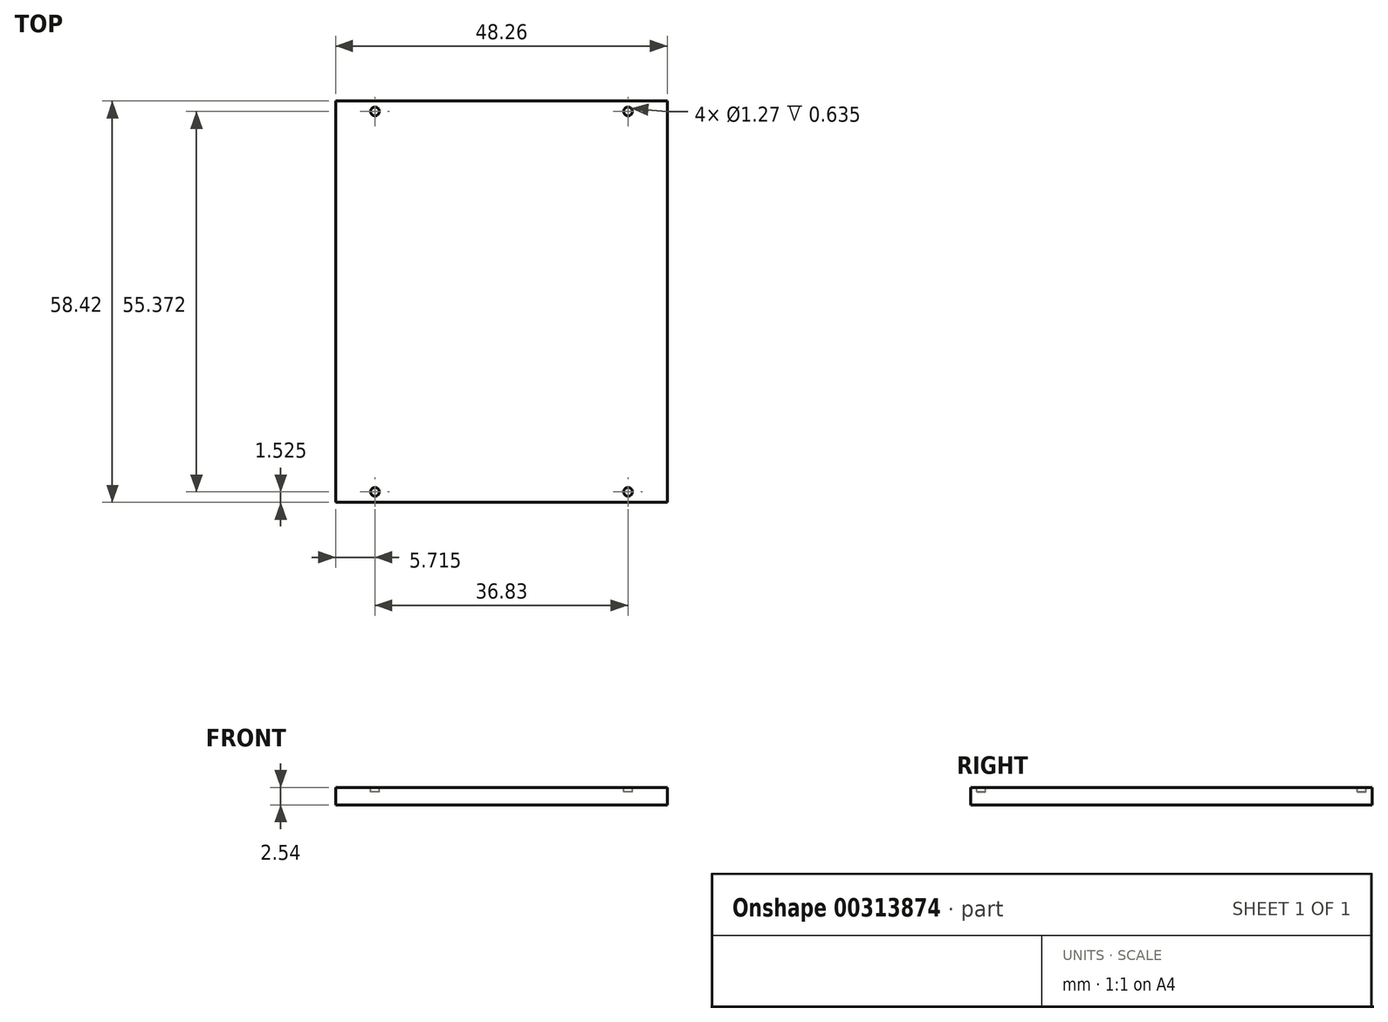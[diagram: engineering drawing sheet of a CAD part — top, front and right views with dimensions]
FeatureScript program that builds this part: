
annotation { "Feature Type Name" : "Feature", "Feature Type Description" : "" }
export const myFeature = defineFeature(function(context is Context, id is Id, definition is map)
    precondition{}
    {
        {
            var Q0;
            Q0=qCreatedBy(makeId("Top.planeOp"),FACE);
            var sketch = newSketch(context, id + "F0", { "sketchPlane" : qUnion([Q0])});
            skLineSegment(sketch, "E0.bottom", {"start": v(-22.14, 39.8) * mm, "end": v(26.12, 39.8) * mm});
            skLineSegment(sketch, "E0.top", {"start": v(-22.14, -18.62) * mm, "end": v(26.12, -18.62) * mm});
            skLineSegment(sketch, "E0.left", {"start": v(-22.14, 39.8) * mm, "end": v(-22.14, -18.62) * mm});
            skLineSegment(sketch, "E0.right", {"start": v(26.12, 39.8) * mm, "end": v(26.12, -18.62) * mm});
            skSolve(sketch);
        }
        {
            var Q0;
            Q0=makeQuery(id+"F0.imprint","IMPRINT",FACE,{"disambiguationData":[TD([[makeQuery(id+"F0.imprint","IMPRINT",EDGE,{"derivedFrom":sQuery(id+"F0.wireOp",EDGE,"E0.bottom")}),-1.0]])]});
            extrude(context, id + "F1", {"entities" : qUnion([Q0]), "depth" : 2.54 * mm});
        }
        {
            var Q0;
            Q0=makeQuery(id+"F1.opExtrude","CAP_FACE",FACE,{"disambiguationData":[OSD([sQuery(id+"F0.wireOp",EDGE,"E0.bottom"),sQuery(id+"F0.wireOp",EDGE,"E0.top"),sQuery(id+"F0.wireOp",EDGE,"E0.left"),sQuery(id+"F0.wireOp",EDGE,"E0.right")])],"isStart":false});
            var sketch = newSketch(context, id + "F2", { "sketchPlane" : qUnion([Q0])});
            skCircle(sketch, "E1", {"center": v(20.4, 38.28) * mm, "radius": 0.64 * mm});
            skSolve(sketch);
        }
        {
            var Q0;
            Q0=makeQuery(id+"F2.imprint","IMPRINT",FACE,{"disambiguationData":[TD([[makeQuery(id+"F2.imprint","IMPRINT",EDGE,{"derivedFrom":sQuery(id+"F2.wireOp",EDGE,"E1")}),1.0]])]});
            extrude(context, id + "F3", {"entities" : qUnion([Q0]), "operationType" : NewBodyOperationType.REMOVE, "oppositeDirection" : true, "depth" : 0.64 * mm});
        }
        {
            var Q0;
            Q0=makeQuery(id+"F1.opExtrude","CAP_FACE",FACE,{"disambiguationData":[OSD([sQuery(id+"F0.wireOp",EDGE,"E0.bottom"),sQuery(id+"F0.wireOp",EDGE,"E0.top"),sQuery(id+"F0.wireOp",EDGE,"E0.left"),sQuery(id+"F0.wireOp",EDGE,"E0.right")])],"isStart":false});
            var sketch = newSketch(context, id + "F4", { "sketchPlane" : qUnion([Q0])});
            skCircle(sketch, "E2", {"center": v(-16.42, 38.28) * mm, "radius": 0.64 * mm});
            skSolve(sketch);
        }
        {
            var Q0;
            Q0=makeQuery(id+"F4.imprint","IMPRINT",FACE,{"disambiguationData":[TD([[makeQuery(id+"F4.imprint","IMPRINT",EDGE,{"derivedFrom":sQuery(id+"F4.wireOp",EDGE,"E2")}),-1.0]])]});
            var sketch = newSketch(context, id + "F5", { "sketchPlane" : qUnion([Q0])});
            skCircle(sketch, "E3", {"center": v(-16.42, -17.1) * mm, "radius": 0.64 * mm});
            skSolve(sketch);
        }
        {
            var Q0;
            Q0=makeQuery(id+"F4.imprint","IMPRINT",FACE,{"disambiguationData":[TD([[makeQuery(id+"F4.imprint","IMPRINT",EDGE,{"derivedFrom":sQuery(id+"F4.wireOp",EDGE,"E2")}),-1.0]])]});
            var sketch = newSketch(context, id + "F6", { "sketchPlane" : qUnion([Q0])});
            skCircle(sketch, "E4", {"center": v(20.4, -17.1) * mm, "radius": 0.64 * mm});
            skSolve(sketch);
        }
        {
            var Q0;
            Q0=makeQuery(id+"F4.imprint","IMPRINT",FACE,{"disambiguationData":[TD([[makeQuery(id+"F4.imprint","IMPRINT",EDGE,{"derivedFrom":sQuery(id+"F4.wireOp",EDGE,"E2")}),1.0]])]});
            extrude(context, id + "F7", {"entities" : qUnion([Q0]), "operationType" : NewBodyOperationType.REMOVE, "oppositeDirection" : true, "depth" : 0.64 * mm});
        }
        {
            var Q0;
            Q0=makeQuery(id+"F6.imprint","IMPRINT",FACE,{"disambiguationData":[TD([[makeQuery(id+"F6.imprint","IMPRINT",EDGE,{"derivedFrom":sQuery(id+"F6.wireOp",EDGE,"E4")}),1.0]])]});
            extrude(context, id + "F8", {"entities" : qUnion([Q0]), "operationType" : NewBodyOperationType.REMOVE, "oppositeDirection" : true, "depth" : 0.64 * mm});
        }
        {
            var Q0;
            Q0=makeQuery(id+"F5.imprint","IMPRINT",FACE,{"disambiguationData":[TD([[makeQuery(id+"F5.imprint","IMPRINT",EDGE,{"derivedFrom":sQuery(id+"F5.wireOp",EDGE,"E3")}),1.0]])]});
            extrude(context, id + "F9", {"entities" : qUnion([Q0]), "operationType" : NewBodyOperationType.REMOVE, "oppositeDirection" : true, "depth" : 0.64 * mm});
        }
    });
